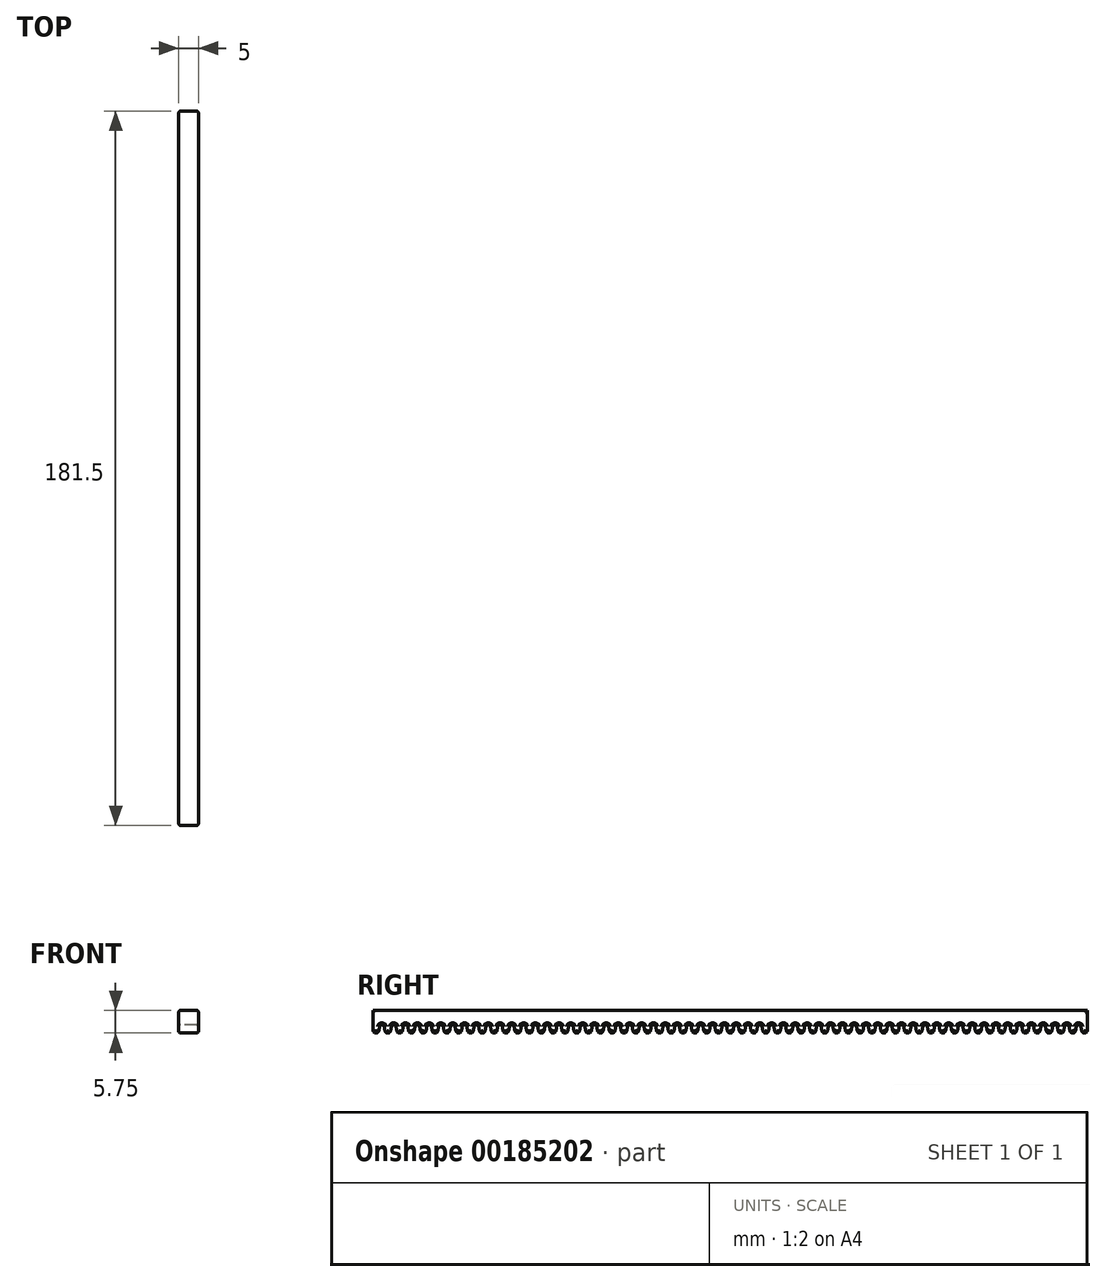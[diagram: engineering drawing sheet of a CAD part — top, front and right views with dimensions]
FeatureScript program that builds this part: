
annotation { "Feature Type Name" : "Feature", "Feature Type Description" : "" }
export const myFeature = defineFeature(function(context is Context, id is Id, definition is map)
    precondition{}
    {
        {
            var Q0;
            Q0=qCreatedBy(makeId("Right.planeOp"),FACE);
            var sketch = newSketch(context, id + "F0", { "sketchPlane" : qUnion([Q0])});
            skArc(sketch, "E0", {"start": v(-0.75, 0) * mm, "mid": v(-0.06, -0.75) * mm, "end": v(0.74, -0.13) * mm});
            skArc(sketch, "E1", {"start": v(2.1, 0.85) * mm, "mid": v(1.5, 1.35) * mm, "end": v(0.9, 0.85) * mm});
            skLineSegment(sketch, "E2", {"start": v(0.9, 0.85) * mm, "end": v(0.74, -0.13) * mm});
            skArc(sketch, "E3", {"start": v(2.26, -0.13) * mm, "mid": v(3, -0.75) * mm, "end": v(3.74, -0.13) * mm});
            skArc(sketch, "E4", {"start": v(5.1, 0.85) * mm, "mid": v(4.5, 1.35) * mm, "end": v(3.9, 0.85) * mm});
            skArc(sketch, "E5", {"start": v(5.26, -0.13) * mm, "mid": v(6.06, -0.75) * mm, "end": v(6.75, 0) * mm});
            skLineSegment(sketch, "E6", {"start": v(2.1, 0.85) * mm, "end": v(2.26, -0.13) * mm});
            skLineSegment(sketch, "E7", {"start": v(3.9, 0.85) * mm, "end": v(3.74, -0.13) * mm});
            skLineSegment(sketch, "E8", {"start": v(5.1, 0.85) * mm, "end": v(5.26, -0.13) * mm});
            skLineSegment(sketch, "E9", {"start": v(-0.75, 0) * mm, "end": v(-0.75, 5) * mm});
            skLineSegment(sketch, "E10", {"start": v(-0.75, 5) * mm, "end": v(180.75, 5) * mm});
            skArc(sketch, "E11.1.0.0", {"start": v(11.1, 0.85) * mm, "mid": v(10.5, 1.35) * mm, "end": v(9.9, 0.85) * mm});
            skLineSegment(sketch, "E11.1.0.1", {"start": v(11.1, 0.85) * mm, "end": v(11.26, -0.13) * mm});
            skArc(sketch, "E11.1.0.2", {"start": v(5.25, 0) * mm, "mid": v(5.94, -0.75) * mm, "end": v(6.74, -0.13) * mm});
            skArc(sketch, "E11.1.0.3", {"start": v(8.26, -0.13) * mm, "mid": v(9, -0.75) * mm, "end": v(9.74, -0.13) * mm});
            skLineSegment(sketch, "E11.1.0.4", {"start": v(8.1, 0.85) * mm, "end": v(8.26, -0.13) * mm});
            skArc(sketch, "E11.1.0.5", {"start": v(8.1, 0.85) * mm, "mid": v(7.5, 1.35) * mm, "end": v(6.9, 0.85) * mm});
            skLineSegment(sketch, "E11.1.0.6", {"start": v(9.9, 0.85) * mm, "end": v(9.74, -0.13) * mm});
            skArc(sketch, "E11.1.0.7", {"start": v(11.26, -0.13) * mm, "mid": v(12.06, -0.75) * mm, "end": v(12.75, 0) * mm});
            skLineSegment(sketch, "E11.1.0.8", {"start": v(6.9, 0.85) * mm, "end": v(6.74, -0.13) * mm});
            skArc(sketch, "E11.2.0.0", {"start": v(17.1, 0.85) * mm, "mid": v(16.5, 1.35) * mm, "end": v(15.9, 0.85) * mm});
            skLineSegment(sketch, "E11.2.0.1", {"start": v(17.1, 0.85) * mm, "end": v(17.26, -0.13) * mm});
            skArc(sketch, "E11.2.0.2", {"start": v(11.25, 0) * mm, "mid": v(11.94, -0.75) * mm, "end": v(12.74, -0.13) * mm});
            skArc(sketch, "E11.2.0.3", {"start": v(14.26, -0.13) * mm, "mid": v(15, -0.75) * mm, "end": v(15.74, -0.13) * mm});
            skLineSegment(sketch, "E11.2.0.4", {"start": v(14.1, 0.85) * mm, "end": v(14.26, -0.13) * mm});
            skArc(sketch, "E11.2.0.5", {"start": v(14.1, 0.85) * mm, "mid": v(13.5, 1.35) * mm, "end": v(12.9, 0.85) * mm});
            skLineSegment(sketch, "E11.2.0.6", {"start": v(15.9, 0.85) * mm, "end": v(15.74, -0.13) * mm});
            skArc(sketch, "E11.2.0.7", {"start": v(17.26, -0.13) * mm, "mid": v(18.06, -0.75) * mm, "end": v(18.75, 0) * mm});
            skLineSegment(sketch, "E11.2.0.8", {"start": v(12.9, 0.85) * mm, "end": v(12.74, -0.13) * mm});
            skArc(sketch, "E11.3.0.0", {"start": v(23.1, 0.85) * mm, "mid": v(22.5, 1.35) * mm, "end": v(21.9, 0.85) * mm});
            skLineSegment(sketch, "E11.3.0.1", {"start": v(23.1, 0.85) * mm, "end": v(23.26, -0.13) * mm});
            skArc(sketch, "E11.3.0.2", {"start": v(17.25, 0) * mm, "mid": v(17.94, -0.75) * mm, "end": v(18.74, -0.13) * mm});
            skArc(sketch, "E11.3.0.3", {"start": v(20.26, -0.13) * mm, "mid": v(21, -0.75) * mm, "end": v(21.74, -0.13) * mm});
            skLineSegment(sketch, "E11.3.0.4", {"start": v(20.1, 0.85) * mm, "end": v(20.26, -0.13) * mm});
            skArc(sketch, "E11.3.0.5", {"start": v(20.1, 0.85) * mm, "mid": v(19.5, 1.35) * mm, "end": v(18.9, 0.85) * mm});
            skLineSegment(sketch, "E11.3.0.6", {"start": v(21.9, 0.85) * mm, "end": v(21.74, -0.13) * mm});
            skArc(sketch, "E11.3.0.7", {"start": v(23.26, -0.13) * mm, "mid": v(24.06, -0.75) * mm, "end": v(24.75, 0) * mm});
            skLineSegment(sketch, "E11.3.0.8", {"start": v(18.9, 0.85) * mm, "end": v(18.74, -0.13) * mm});
            skArc(sketch, "E11.4.0.0", {"start": v(29.1, 0.85) * mm, "mid": v(28.5, 1.35) * mm, "end": v(27.9, 0.85) * mm});
            skLineSegment(sketch, "E11.4.0.1", {"start": v(29.1, 0.85) * mm, "end": v(29.26, -0.13) * mm});
            skArc(sketch, "E11.4.0.2", {"start": v(23.25, 0) * mm, "mid": v(23.94, -0.75) * mm, "end": v(24.74, -0.13) * mm});
            skArc(sketch, "E11.4.0.3", {"start": v(26.26, -0.13) * mm, "mid": v(27, -0.75) * mm, "end": v(27.74, -0.13) * mm});
            skLineSegment(sketch, "E11.4.0.4", {"start": v(26.1, 0.85) * mm, "end": v(26.26, -0.13) * mm});
            skArc(sketch, "E11.4.0.5", {"start": v(26.1, 0.85) * mm, "mid": v(25.5, 1.35) * mm, "end": v(24.9, 0.85) * mm});
            skLineSegment(sketch, "E11.4.0.6", {"start": v(27.9, 0.85) * mm, "end": v(27.74, -0.13) * mm});
            skArc(sketch, "E11.4.0.7", {"start": v(29.26, -0.13) * mm, "mid": v(30.06, -0.75) * mm, "end": v(30.75, 0) * mm});
            skLineSegment(sketch, "E11.4.0.8", {"start": v(24.9, 0.85) * mm, "end": v(24.74, -0.13) * mm});
            skArc(sketch, "E11.5.0.0", {"start": v(35.1, 0.85) * mm, "mid": v(34.5, 1.35) * mm, "end": v(33.9, 0.85) * mm});
            skLineSegment(sketch, "E11.5.0.1", {"start": v(35.1, 0.85) * mm, "end": v(35.26, -0.13) * mm});
            skArc(sketch, "E11.5.0.2", {"start": v(29.25, 0) * mm, "mid": v(29.94, -0.75) * mm, "end": v(30.74, -0.13) * mm});
            skArc(sketch, "E11.5.0.3", {"start": v(32.26, -0.13) * mm, "mid": v(33, -0.75) * mm, "end": v(33.74, -0.13) * mm});
            skLineSegment(sketch, "E11.5.0.4", {"start": v(32.1, 0.85) * mm, "end": v(32.26, -0.13) * mm});
            skArc(sketch, "E11.5.0.5", {"start": v(32.1, 0.85) * mm, "mid": v(31.5, 1.35) * mm, "end": v(30.9, 0.85) * mm});
            skLineSegment(sketch, "E11.5.0.6", {"start": v(33.9, 0.85) * mm, "end": v(33.74, -0.13) * mm});
            skArc(sketch, "E11.5.0.7", {"start": v(35.26, -0.13) * mm, "mid": v(36.06, -0.75) * mm, "end": v(36.75, 0) * mm});
            skLineSegment(sketch, "E11.5.0.8", {"start": v(30.9, 0.85) * mm, "end": v(30.74, -0.13) * mm});
            skArc(sketch, "E11.6.0.0", {"start": v(41.1, 0.85) * mm, "mid": v(40.5, 1.35) * mm, "end": v(39.9, 0.85) * mm});
            skLineSegment(sketch, "E11.6.0.1", {"start": v(41.1, 0.85) * mm, "end": v(41.26, -0.13) * mm});
            skArc(sketch, "E11.6.0.2", {"start": v(35.25, 0) * mm, "mid": v(35.94, -0.75) * mm, "end": v(36.74, -0.13) * mm});
            skArc(sketch, "E11.6.0.3", {"start": v(38.26, -0.13) * mm, "mid": v(39, -0.75) * mm, "end": v(39.74, -0.13) * mm});
            skLineSegment(sketch, "E11.6.0.4", {"start": v(38.1, 0.85) * mm, "end": v(38.26, -0.13) * mm});
            skArc(sketch, "E11.6.0.5", {"start": v(38.1, 0.85) * mm, "mid": v(37.5, 1.35) * mm, "end": v(36.9, 0.85) * mm});
            skLineSegment(sketch, "E11.6.0.6", {"start": v(39.9, 0.85) * mm, "end": v(39.74, -0.13) * mm});
            skArc(sketch, "E11.6.0.7", {"start": v(41.26, -0.13) * mm, "mid": v(42.06, -0.75) * mm, "end": v(42.75, 0) * mm});
            skLineSegment(sketch, "E11.6.0.8", {"start": v(36.9, 0.85) * mm, "end": v(36.74, -0.13) * mm});
            skArc(sketch, "E11.7.0.0", {"start": v(47.1, 0.85) * mm, "mid": v(46.5, 1.35) * mm, "end": v(45.9, 0.85) * mm});
            skLineSegment(sketch, "E11.7.0.1", {"start": v(47.1, 0.85) * mm, "end": v(47.26, -0.13) * mm});
            skArc(sketch, "E11.7.0.2", {"start": v(41.25, 0) * mm, "mid": v(41.94, -0.75) * mm, "end": v(42.74, -0.13) * mm});
            skArc(sketch, "E11.7.0.3", {"start": v(44.26, -0.13) * mm, "mid": v(45, -0.75) * mm, "end": v(45.74, -0.13) * mm});
            skLineSegment(sketch, "E11.7.0.4", {"start": v(44.1, 0.85) * mm, "end": v(44.26, -0.13) * mm});
            skArc(sketch, "E11.7.0.5", {"start": v(44.1, 0.85) * mm, "mid": v(43.5, 1.35) * mm, "end": v(42.9, 0.85) * mm});
            skLineSegment(sketch, "E11.7.0.6", {"start": v(45.9, 0.85) * mm, "end": v(45.74, -0.13) * mm});
            skArc(sketch, "E11.7.0.7", {"start": v(47.26, -0.13) * mm, "mid": v(48.06, -0.75) * mm, "end": v(48.75, 0) * mm});
            skLineSegment(sketch, "E11.7.0.8", {"start": v(42.9, 0.85) * mm, "end": v(42.74, -0.13) * mm});
            skArc(sketch, "E11.8.0.0", {"start": v(53.1, 0.85) * mm, "mid": v(52.5, 1.35) * mm, "end": v(51.9, 0.85) * mm});
            skLineSegment(sketch, "E11.8.0.1", {"start": v(53.1, 0.85) * mm, "end": v(53.26, -0.13) * mm});
            skArc(sketch, "E11.8.0.2", {"start": v(47.25, 0) * mm, "mid": v(47.94, -0.75) * mm, "end": v(48.74, -0.13) * mm});
            skArc(sketch, "E11.8.0.3", {"start": v(50.26, -0.13) * mm, "mid": v(51, -0.75) * mm, "end": v(51.74, -0.13) * mm});
            skLineSegment(sketch, "E11.8.0.4", {"start": v(50.1, 0.85) * mm, "end": v(50.26, -0.13) * mm});
            skArc(sketch, "E11.8.0.5", {"start": v(50.1, 0.85) * mm, "mid": v(49.5, 1.35) * mm, "end": v(48.9, 0.85) * mm});
            skLineSegment(sketch, "E11.8.0.6", {"start": v(51.9, 0.85) * mm, "end": v(51.74, -0.13) * mm});
            skArc(sketch, "E11.8.0.7", {"start": v(53.26, -0.13) * mm, "mid": v(54.06, -0.75) * mm, "end": v(54.75, 0) * mm});
            skLineSegment(sketch, "E11.8.0.8", {"start": v(48.9, 0.85) * mm, "end": v(48.74, -0.13) * mm});
            skArc(sketch, "E11.9.0.0", {"start": v(59.1, 0.85) * mm, "mid": v(58.5, 1.35) * mm, "end": v(57.9, 0.85) * mm});
            skLineSegment(sketch, "E11.9.0.1", {"start": v(59.1, 0.85) * mm, "end": v(59.26, -0.13) * mm});
            skArc(sketch, "E11.9.0.2", {"start": v(53.25, 0) * mm, "mid": v(53.94, -0.75) * mm, "end": v(54.74, -0.13) * mm});
            skArc(sketch, "E11.9.0.3", {"start": v(56.26, -0.13) * mm, "mid": v(57, -0.75) * mm, "end": v(57.74, -0.13) * mm});
            skLineSegment(sketch, "E11.9.0.4", {"start": v(56.1, 0.85) * mm, "end": v(56.26, -0.13) * mm});
            skArc(sketch, "E11.9.0.5", {"start": v(56.1, 0.85) * mm, "mid": v(55.5, 1.35) * mm, "end": v(54.9, 0.85) * mm});
            skLineSegment(sketch, "E11.9.0.6", {"start": v(57.9, 0.85) * mm, "end": v(57.74, -0.13) * mm});
            skArc(sketch, "E11.9.0.7", {"start": v(59.26, -0.13) * mm, "mid": v(60.06, -0.75) * mm, "end": v(60.75, 0) * mm});
            skLineSegment(sketch, "E11.9.0.8", {"start": v(54.9, 0.85) * mm, "end": v(54.74, -0.13) * mm});
            skArc(sketch, "E11.10.0.0", {"start": v(65.1, 0.85) * mm, "mid": v(64.5, 1.35) * mm, "end": v(63.9, 0.85) * mm});
            skLineSegment(sketch, "E11.10.0.1", {"start": v(65.1, 0.85) * mm, "end": v(65.26, -0.13) * mm});
            skArc(sketch, "E11.10.0.2", {"start": v(59.25, 0) * mm, "mid": v(59.94, -0.75) * mm, "end": v(60.74, -0.13) * mm});
            skArc(sketch, "E11.10.0.3", {"start": v(62.26, -0.13) * mm, "mid": v(63, -0.75) * mm, "end": v(63.74, -0.13) * mm});
            skLineSegment(sketch, "E11.10.0.4", {"start": v(62.1, 0.85) * mm, "end": v(62.26, -0.13) * mm});
            skArc(sketch, "E11.10.0.5", {"start": v(62.1, 0.85) * mm, "mid": v(61.5, 1.35) * mm, "end": v(60.9, 0.85) * mm});
            skLineSegment(sketch, "E11.10.0.6", {"start": v(63.9, 0.85) * mm, "end": v(63.74, -0.13) * mm});
            skArc(sketch, "E11.10.0.7", {"start": v(65.26, -0.13) * mm, "mid": v(66.06, -0.75) * mm, "end": v(66.75, 0) * mm});
            skLineSegment(sketch, "E11.10.0.8", {"start": v(60.9, 0.85) * mm, "end": v(60.74, -0.13) * mm});
            skArc(sketch, "E11.11.0.0", {"start": v(71.1, 0.85) * mm, "mid": v(70.5, 1.35) * mm, "end": v(69.9, 0.85) * mm});
            skLineSegment(sketch, "E11.11.0.1", {"start": v(71.1, 0.85) * mm, "end": v(71.26, -0.13) * mm});
            skArc(sketch, "E11.11.0.2", {"start": v(65.25, 0) * mm, "mid": v(65.94, -0.75) * mm, "end": v(66.74, -0.13) * mm});
            skArc(sketch, "E11.11.0.3", {"start": v(68.26, -0.13) * mm, "mid": v(69, -0.75) * mm, "end": v(69.74, -0.13) * mm});
            skLineSegment(sketch, "E11.11.0.4", {"start": v(68.1, 0.85) * mm, "end": v(68.26, -0.13) * mm});
            skArc(sketch, "E11.11.0.5", {"start": v(68.1, 0.85) * mm, "mid": v(67.5, 1.35) * mm, "end": v(66.9, 0.85) * mm});
            skLineSegment(sketch, "E11.11.0.6", {"start": v(69.9, 0.85) * mm, "end": v(69.74, -0.13) * mm});
            skArc(sketch, "E11.11.0.7", {"start": v(71.26, -0.13) * mm, "mid": v(72.06, -0.75) * mm, "end": v(72.75, 0) * mm});
            skLineSegment(sketch, "E11.11.0.8", {"start": v(66.9, 0.85) * mm, "end": v(66.74, -0.13) * mm});
            skArc(sketch, "E11.12.0.0", {"start": v(77.1, 0.85) * mm, "mid": v(76.5, 1.35) * mm, "end": v(75.9, 0.85) * mm});
            skLineSegment(sketch, "E11.12.0.1", {"start": v(77.1, 0.85) * mm, "end": v(77.26, -0.13) * mm});
            skArc(sketch, "E11.12.0.2", {"start": v(71.25, 0) * mm, "mid": v(71.94, -0.75) * mm, "end": v(72.74, -0.13) * mm});
            skArc(sketch, "E11.12.0.3", {"start": v(74.26, -0.13) * mm, "mid": v(75, -0.75) * mm, "end": v(75.74, -0.13) * mm});
            skLineSegment(sketch, "E11.12.0.4", {"start": v(74.1, 0.85) * mm, "end": v(74.26, -0.13) * mm});
            skArc(sketch, "E11.12.0.5", {"start": v(74.1, 0.85) * mm, "mid": v(73.5, 1.35) * mm, "end": v(72.9, 0.85) * mm});
            skLineSegment(sketch, "E11.12.0.6", {"start": v(75.9, 0.85) * mm, "end": v(75.74, -0.13) * mm});
            skArc(sketch, "E11.12.0.7", {"start": v(77.26, -0.13) * mm, "mid": v(78.06, -0.75) * mm, "end": v(78.75, 0) * mm});
            skLineSegment(sketch, "E11.12.0.8", {"start": v(72.9, 0.85) * mm, "end": v(72.74, -0.13) * mm});
            skArc(sketch, "E11.13.0.0", {"start": v(83.1, 0.85) * mm, "mid": v(82.5, 1.35) * mm, "end": v(81.9, 0.85) * mm});
            skLineSegment(sketch, "E11.13.0.1", {"start": v(83.1, 0.85) * mm, "end": v(83.26, -0.13) * mm});
            skArc(sketch, "E11.13.0.2", {"start": v(77.25, 0) * mm, "mid": v(77.94, -0.75) * mm, "end": v(78.74, -0.13) * mm});
            skArc(sketch, "E11.13.0.3", {"start": v(80.26, -0.13) * mm, "mid": v(81, -0.75) * mm, "end": v(81.74, -0.13) * mm});
            skLineSegment(sketch, "E11.13.0.4", {"start": v(80.1, 0.85) * mm, "end": v(80.26, -0.13) * mm});
            skArc(sketch, "E11.13.0.5", {"start": v(80.1, 0.85) * mm, "mid": v(79.5, 1.35) * mm, "end": v(78.9, 0.85) * mm});
            skLineSegment(sketch, "E11.13.0.6", {"start": v(81.9, 0.85) * mm, "end": v(81.74, -0.13) * mm});
            skArc(sketch, "E11.13.0.7", {"start": v(83.26, -0.13) * mm, "mid": v(84.06, -0.75) * mm, "end": v(84.75, 0) * mm});
            skLineSegment(sketch, "E11.13.0.8", {"start": v(78.9, 0.85) * mm, "end": v(78.74, -0.13) * mm});
            skArc(sketch, "E11.14.0.0", {"start": v(89.1, 0.85) * mm, "mid": v(88.5, 1.35) * mm, "end": v(87.9, 0.85) * mm});
            skLineSegment(sketch, "E11.14.0.1", {"start": v(89.1, 0.85) * mm, "end": v(89.26, -0.13) * mm});
            skArc(sketch, "E11.14.0.2", {"start": v(83.25, 0) * mm, "mid": v(83.94, -0.75) * mm, "end": v(84.74, -0.13) * mm});
            skArc(sketch, "E11.14.0.3", {"start": v(86.26, -0.13) * mm, "mid": v(87, -0.75) * mm, "end": v(87.74, -0.13) * mm});
            skLineSegment(sketch, "E11.14.0.4", {"start": v(86.1, 0.85) * mm, "end": v(86.26, -0.13) * mm});
            skArc(sketch, "E11.14.0.5", {"start": v(86.1, 0.85) * mm, "mid": v(85.5, 1.35) * mm, "end": v(84.9, 0.85) * mm});
            skLineSegment(sketch, "E11.14.0.6", {"start": v(87.9, 0.85) * mm, "end": v(87.74, -0.13) * mm});
            skArc(sketch, "E11.14.0.7", {"start": v(89.26, -0.13) * mm, "mid": v(90.06, -0.75) * mm, "end": v(90.75, 0) * mm});
            skLineSegment(sketch, "E11.14.0.8", {"start": v(84.9, 0.85) * mm, "end": v(84.74, -0.13) * mm});
            skArc(sketch, "E11.15.0.0", {"start": v(95.1, 0.85) * mm, "mid": v(94.5, 1.35) * mm, "end": v(93.9, 0.85) * mm});
            skLineSegment(sketch, "E11.15.0.1", {"start": v(95.1, 0.85) * mm, "end": v(95.26, -0.13) * mm});
            skArc(sketch, "E11.15.0.2", {"start": v(89.25, 0) * mm, "mid": v(89.94, -0.75) * mm, "end": v(90.74, -0.13) * mm});
            skArc(sketch, "E11.15.0.3", {"start": v(92.26, -0.13) * mm, "mid": v(93, -0.75) * mm, "end": v(93.74, -0.13) * mm});
            skLineSegment(sketch, "E11.15.0.4", {"start": v(92.1, 0.85) * mm, "end": v(92.26, -0.13) * mm});
            skArc(sketch, "E11.15.0.5", {"start": v(92.1, 0.85) * mm, "mid": v(91.5, 1.35) * mm, "end": v(90.9, 0.85) * mm});
            skLineSegment(sketch, "E11.15.0.6", {"start": v(93.9, 0.85) * mm, "end": v(93.74, -0.13) * mm});
            skArc(sketch, "E11.15.0.7", {"start": v(95.26, -0.13) * mm, "mid": v(96.06, -0.75) * mm, "end": v(96.75, 0) * mm});
            skLineSegment(sketch, "E11.15.0.8", {"start": v(90.9, 0.85) * mm, "end": v(90.74, -0.13) * mm});
            skArc(sketch, "E11.16.0.0", {"start": v(101.1, 0.85) * mm, "mid": v(100.5, 1.35) * mm, "end": v(99.9, 0.85) * mm});
            skLineSegment(sketch, "E11.16.0.1", {"start": v(101.1, 0.85) * mm, "end": v(101.26, -0.13) * mm});
            skArc(sketch, "E11.16.0.2", {"start": v(95.25, 0) * mm, "mid": v(95.94, -0.75) * mm, "end": v(96.74, -0.13) * mm});
            skArc(sketch, "E11.16.0.3", {"start": v(98.26, -0.13) * mm, "mid": v(99, -0.75) * mm, "end": v(99.74, -0.13) * mm});
            skLineSegment(sketch, "E11.16.0.4", {"start": v(98.1, 0.85) * mm, "end": v(98.26, -0.13) * mm});
            skArc(sketch, "E11.16.0.5", {"start": v(98.1, 0.85) * mm, "mid": v(97.5, 1.35) * mm, "end": v(96.9, 0.85) * mm});
            skLineSegment(sketch, "E11.16.0.6", {"start": v(99.9, 0.85) * mm, "end": v(99.74, -0.13) * mm});
            skArc(sketch, "E11.16.0.7", {"start": v(101.26, -0.13) * mm, "mid": v(102.06, -0.75) * mm, "end": v(102.75, 0) * mm});
            skLineSegment(sketch, "E11.16.0.8", {"start": v(96.9, 0.85) * mm, "end": v(96.74, -0.13) * mm});
            skArc(sketch, "E11.17.0.0", {"start": v(107.1, 0.85) * mm, "mid": v(106.5, 1.35) * mm, "end": v(105.9, 0.85) * mm});
            skLineSegment(sketch, "E11.17.0.1", {"start": v(107.1, 0.85) * mm, "end": v(107.26, -0.13) * mm});
            skArc(sketch, "E11.17.0.2", {"start": v(101.25, 0) * mm, "mid": v(101.94, -0.75) * mm, "end": v(102.74, -0.13) * mm});
            skArc(sketch, "E11.17.0.3", {"start": v(104.26, -0.13) * mm, "mid": v(105, -0.75) * mm, "end": v(105.74, -0.13) * mm});
            skLineSegment(sketch, "E11.17.0.4", {"start": v(104.1, 0.85) * mm, "end": v(104.26, -0.13) * mm});
            skArc(sketch, "E11.17.0.5", {"start": v(104.1, 0.85) * mm, "mid": v(103.5, 1.35) * mm, "end": v(102.9, 0.85) * mm});
            skLineSegment(sketch, "E11.17.0.6", {"start": v(105.9, 0.85) * mm, "end": v(105.74, -0.13) * mm});
            skArc(sketch, "E11.17.0.7", {"start": v(107.26, -0.13) * mm, "mid": v(108.06, -0.75) * mm, "end": v(108.75, 0) * mm});
            skLineSegment(sketch, "E11.17.0.8", {"start": v(102.9, 0.85) * mm, "end": v(102.74, -0.13) * mm});
            skArc(sketch, "E11.18.0.0", {"start": v(113.1, 0.85) * mm, "mid": v(112.5, 1.35) * mm, "end": v(111.9, 0.85) * mm});
            skLineSegment(sketch, "E11.18.0.1", {"start": v(113.1, 0.85) * mm, "end": v(113.26, -0.13) * mm});
            skArc(sketch, "E11.18.0.2", {"start": v(107.25, 0) * mm, "mid": v(107.94, -0.75) * mm, "end": v(108.74, -0.13) * mm});
            skArc(sketch, "E11.18.0.3", {"start": v(110.26, -0.13) * mm, "mid": v(111, -0.75) * mm, "end": v(111.74, -0.13) * mm});
            skLineSegment(sketch, "E11.18.0.4", {"start": v(110.1, 0.85) * mm, "end": v(110.26, -0.13) * mm});
            skArc(sketch, "E11.18.0.5", {"start": v(110.1, 0.85) * mm, "mid": v(109.5, 1.35) * mm, "end": v(108.9, 0.85) * mm});
            skLineSegment(sketch, "E11.18.0.6", {"start": v(111.9, 0.85) * mm, "end": v(111.74, -0.13) * mm});
            skArc(sketch, "E11.18.0.7", {"start": v(113.26, -0.13) * mm, "mid": v(114.06, -0.75) * mm, "end": v(114.75, 0) * mm});
            skLineSegment(sketch, "E11.18.0.8", {"start": v(108.9, 0.85) * mm, "end": v(108.74, -0.13) * mm});
            skArc(sketch, "E11.19.0.0", {"start": v(119.1, 0.85) * mm, "mid": v(118.5, 1.35) * mm, "end": v(117.9, 0.85) * mm});
            skLineSegment(sketch, "E11.19.0.1", {"start": v(119.1, 0.85) * mm, "end": v(119.26, -0.13) * mm});
            skArc(sketch, "E11.19.0.2", {"start": v(113.25, 0) * mm, "mid": v(113.94, -0.75) * mm, "end": v(114.74, -0.13) * mm});
            skArc(sketch, "E11.19.0.3", {"start": v(116.26, -0.13) * mm, "mid": v(117, -0.75) * mm, "end": v(117.74, -0.13) * mm});
            skLineSegment(sketch, "E11.19.0.4", {"start": v(116.1, 0.85) * mm, "end": v(116.26, -0.13) * mm});
            skArc(sketch, "E11.19.0.5", {"start": v(116.1, 0.85) * mm, "mid": v(115.5, 1.35) * mm, "end": v(114.9, 0.85) * mm});
            skLineSegment(sketch, "E11.19.0.6", {"start": v(117.9, 0.85) * mm, "end": v(117.74, -0.13) * mm});
            skArc(sketch, "E11.19.0.7", {"start": v(119.26, -0.13) * mm, "mid": v(120.06, -0.75) * mm, "end": v(120.75, 0) * mm});
            skLineSegment(sketch, "E11.19.0.8", {"start": v(114.9, 0.85) * mm, "end": v(114.74, -0.13) * mm});
            skArc(sketch, "E11.20.0.0", {"start": v(125.1, 0.85) * mm, "mid": v(124.5, 1.35) * mm, "end": v(123.9, 0.85) * mm});
            skLineSegment(sketch, "E11.20.0.1", {"start": v(125.1, 0.85) * mm, "end": v(125.26, -0.13) * mm});
            skArc(sketch, "E11.20.0.2", {"start": v(119.25, 0) * mm, "mid": v(119.94, -0.75) * mm, "end": v(120.74, -0.13) * mm});
            skArc(sketch, "E11.20.0.3", {"start": v(122.26, -0.13) * mm, "mid": v(123, -0.75) * mm, "end": v(123.74, -0.13) * mm});
            skLineSegment(sketch, "E11.20.0.4", {"start": v(122.1, 0.85) * mm, "end": v(122.26, -0.13) * mm});
            skArc(sketch, "E11.20.0.5", {"start": v(122.1, 0.85) * mm, "mid": v(121.5, 1.35) * mm, "end": v(120.9, 0.85) * mm});
            skLineSegment(sketch, "E11.20.0.6", {"start": v(123.9, 0.85) * mm, "end": v(123.74, -0.13) * mm});
            skArc(sketch, "E11.20.0.7", {"start": v(125.26, -0.13) * mm, "mid": v(126.06, -0.75) * mm, "end": v(126.75, 0) * mm});
            skLineSegment(sketch, "E11.20.0.8", {"start": v(120.9, 0.85) * mm, "end": v(120.74, -0.13) * mm});
            skArc(sketch, "E11.21.0.0", {"start": v(131.1, 0.85) * mm, "mid": v(130.5, 1.35) * mm, "end": v(129.9, 0.85) * mm});
            skLineSegment(sketch, "E11.21.0.1", {"start": v(131.1, 0.85) * mm, "end": v(131.26, -0.13) * mm});
            skArc(sketch, "E11.21.0.2", {"start": v(125.25, 0) * mm, "mid": v(125.94, -0.75) * mm, "end": v(126.74, -0.13) * mm});
            skArc(sketch, "E11.21.0.3", {"start": v(128.26, -0.13) * mm, "mid": v(129, -0.75) * mm, "end": v(129.74, -0.13) * mm});
            skLineSegment(sketch, "E11.21.0.4", {"start": v(128.1, 0.85) * mm, "end": v(128.26, -0.13) * mm});
            skArc(sketch, "E11.21.0.5", {"start": v(128.1, 0.85) * mm, "mid": v(127.5, 1.35) * mm, "end": v(126.9, 0.85) * mm});
            skLineSegment(sketch, "E11.21.0.6", {"start": v(129.9, 0.85) * mm, "end": v(129.74, -0.13) * mm});
            skArc(sketch, "E11.21.0.7", {"start": v(131.26, -0.13) * mm, "mid": v(132.06, -0.75) * mm, "end": v(132.75, 0) * mm});
            skLineSegment(sketch, "E11.21.0.8", {"start": v(126.9, 0.85) * mm, "end": v(126.74, -0.13) * mm});
            skArc(sketch, "E11.22.0.0", {"start": v(137.1, 0.85) * mm, "mid": v(136.5, 1.35) * mm, "end": v(135.9, 0.85) * mm});
            skLineSegment(sketch, "E11.22.0.1", {"start": v(137.1, 0.85) * mm, "end": v(137.26, -0.13) * mm});
            skArc(sketch, "E11.22.0.2", {"start": v(131.25, 0) * mm, "mid": v(131.94, -0.75) * mm, "end": v(132.74, -0.13) * mm});
            skArc(sketch, "E11.22.0.3", {"start": v(134.26, -0.13) * mm, "mid": v(135, -0.75) * mm, "end": v(135.74, -0.13) * mm});
            skLineSegment(sketch, "E11.22.0.4", {"start": v(134.1, 0.85) * mm, "end": v(134.26, -0.13) * mm});
            skArc(sketch, "E11.22.0.5", {"start": v(134.1, 0.85) * mm, "mid": v(133.5, 1.35) * mm, "end": v(132.9, 0.85) * mm});
            skLineSegment(sketch, "E11.22.0.6", {"start": v(135.9, 0.85) * mm, "end": v(135.74, -0.13) * mm});
            skArc(sketch, "E11.22.0.7", {"start": v(137.26, -0.13) * mm, "mid": v(138.06, -0.75) * mm, "end": v(138.75, 0) * mm});
            skLineSegment(sketch, "E11.22.0.8", {"start": v(132.9, 0.85) * mm, "end": v(132.74, -0.13) * mm});
            skArc(sketch, "E11.23.0.0", {"start": v(143.1, 0.85) * mm, "mid": v(142.5, 1.35) * mm, "end": v(141.9, 0.85) * mm});
            skLineSegment(sketch, "E11.23.0.1", {"start": v(143.1, 0.85) * mm, "end": v(143.26, -0.13) * mm});
            skArc(sketch, "E11.23.0.2", {"start": v(137.25, 0) * mm, "mid": v(137.94, -0.75) * mm, "end": v(138.74, -0.13) * mm});
            skArc(sketch, "E11.23.0.3", {"start": v(140.26, -0.13) * mm, "mid": v(141, -0.75) * mm, "end": v(141.74, -0.13) * mm});
            skLineSegment(sketch, "E11.23.0.4", {"start": v(140.1, 0.85) * mm, "end": v(140.26, -0.13) * mm});
            skArc(sketch, "E11.23.0.5", {"start": v(140.1, 0.85) * mm, "mid": v(139.5, 1.35) * mm, "end": v(138.9, 0.85) * mm});
            skLineSegment(sketch, "E11.23.0.6", {"start": v(141.9, 0.85) * mm, "end": v(141.74, -0.13) * mm});
            skArc(sketch, "E11.23.0.7", {"start": v(143.26, -0.13) * mm, "mid": v(144.06, -0.75) * mm, "end": v(144.75, 0) * mm});
            skLineSegment(sketch, "E11.23.0.8", {"start": v(138.9, 0.85) * mm, "end": v(138.74, -0.13) * mm});
            skArc(sketch, "E11.24.0.0", {"start": v(149.1, 0.85) * mm, "mid": v(148.5, 1.35) * mm, "end": v(147.9, 0.85) * mm});
            skLineSegment(sketch, "E11.24.0.1", {"start": v(149.1, 0.85) * mm, "end": v(149.26, -0.13) * mm});
            skArc(sketch, "E11.24.0.2", {"start": v(143.25, 0) * mm, "mid": v(143.94, -0.75) * mm, "end": v(144.74, -0.13) * mm});
            skArc(sketch, "E11.24.0.3", {"start": v(146.26, -0.13) * mm, "mid": v(147, -0.75) * mm, "end": v(147.74, -0.13) * mm});
            skLineSegment(sketch, "E11.24.0.4", {"start": v(146.1, 0.85) * mm, "end": v(146.26, -0.13) * mm});
            skArc(sketch, "E11.24.0.5", {"start": v(146.1, 0.85) * mm, "mid": v(145.5, 1.35) * mm, "end": v(144.9, 0.85) * mm});
            skLineSegment(sketch, "E11.24.0.6", {"start": v(147.9, 0.85) * mm, "end": v(147.74, -0.13) * mm});
            skArc(sketch, "E11.24.0.7", {"start": v(149.26, -0.13) * mm, "mid": v(150.06, -0.75) * mm, "end": v(150.75, 0) * mm});
            skLineSegment(sketch, "E11.24.0.8", {"start": v(144.9, 0.85) * mm, "end": v(144.74, -0.13) * mm});
            skArc(sketch, "E11.25.0.0", {"start": v(155.1, 0.85) * mm, "mid": v(154.5, 1.35) * mm, "end": v(153.9, 0.85) * mm});
            skLineSegment(sketch, "E11.25.0.1", {"start": v(155.1, 0.85) * mm, "end": v(155.26, -0.13) * mm});
            skArc(sketch, "E11.25.0.2", {"start": v(149.25, 0) * mm, "mid": v(149.94, -0.75) * mm, "end": v(150.74, -0.13) * mm});
            skArc(sketch, "E11.25.0.3", {"start": v(152.26, -0.13) * mm, "mid": v(153, -0.75) * mm, "end": v(153.74, -0.13) * mm});
            skLineSegment(sketch, "E11.25.0.4", {"start": v(152.1, 0.85) * mm, "end": v(152.26, -0.13) * mm});
            skArc(sketch, "E11.25.0.5", {"start": v(152.1, 0.85) * mm, "mid": v(151.5, 1.35) * mm, "end": v(150.9, 0.85) * mm});
            skLineSegment(sketch, "E11.25.0.6", {"start": v(153.9, 0.85) * mm, "end": v(153.74, -0.13) * mm});
            skArc(sketch, "E11.25.0.7", {"start": v(155.26, -0.13) * mm, "mid": v(156.06, -0.75) * mm, "end": v(156.75, 0) * mm});
            skLineSegment(sketch, "E11.25.0.8", {"start": v(150.9, 0.85) * mm, "end": v(150.74, -0.13) * mm});
            skArc(sketch, "E11.26.0.0", {"start": v(161.1, 0.85) * mm, "mid": v(160.5, 1.35) * mm, "end": v(159.9, 0.85) * mm});
            skLineSegment(sketch, "E11.26.0.1", {"start": v(161.1, 0.85) * mm, "end": v(161.26, -0.13) * mm});
            skArc(sketch, "E11.26.0.2", {"start": v(155.25, 0) * mm, "mid": v(155.94, -0.75) * mm, "end": v(156.74, -0.13) * mm});
            skArc(sketch, "E11.26.0.3", {"start": v(158.26, -0.13) * mm, "mid": v(159, -0.75) * mm, "end": v(159.74, -0.13) * mm});
            skLineSegment(sketch, "E11.26.0.4", {"start": v(158.1, 0.85) * mm, "end": v(158.26, -0.13) * mm});
            skArc(sketch, "E11.26.0.5", {"start": v(158.1, 0.85) * mm, "mid": v(157.5, 1.35) * mm, "end": v(156.9, 0.85) * mm});
            skLineSegment(sketch, "E11.26.0.6", {"start": v(159.9, 0.85) * mm, "end": v(159.74, -0.13) * mm});
            skArc(sketch, "E11.26.0.7", {"start": v(161.26, -0.13) * mm, "mid": v(162.06, -0.75) * mm, "end": v(162.75, 0) * mm});
            skLineSegment(sketch, "E11.26.0.8", {"start": v(156.9, 0.85) * mm, "end": v(156.74, -0.13) * mm});
            skArc(sketch, "E11.27.0.0", {"start": v(167.1, 0.85) * mm, "mid": v(166.5, 1.35) * mm, "end": v(165.9, 0.85) * mm});
            skLineSegment(sketch, "E11.27.0.1", {"start": v(167.1, 0.85) * mm, "end": v(167.26, -0.13) * mm});
            skArc(sketch, "E11.27.0.2", {"start": v(161.25, 0) * mm, "mid": v(161.94, -0.75) * mm, "end": v(162.74, -0.13) * mm});
            skArc(sketch, "E11.27.0.3", {"start": v(164.26, -0.13) * mm, "mid": v(165, -0.75) * mm, "end": v(165.74, -0.13) * mm});
            skLineSegment(sketch, "E11.27.0.4", {"start": v(164.1, 0.85) * mm, "end": v(164.26, -0.13) * mm});
            skArc(sketch, "E11.27.0.5", {"start": v(164.1, 0.85) * mm, "mid": v(163.5, 1.35) * mm, "end": v(162.9, 0.85) * mm});
            skLineSegment(sketch, "E11.27.0.6", {"start": v(165.9, 0.85) * mm, "end": v(165.74, -0.13) * mm});
            skArc(sketch, "E11.27.0.7", {"start": v(167.26, -0.13) * mm, "mid": v(168.06, -0.75) * mm, "end": v(168.75, 0) * mm});
            skLineSegment(sketch, "E11.27.0.8", {"start": v(162.9, 0.85) * mm, "end": v(162.74, -0.13) * mm});
            skArc(sketch, "E11.28.0.0", {"start": v(173.1, 0.85) * mm, "mid": v(172.5, 1.35) * mm, "end": v(171.9, 0.85) * mm});
            skLineSegment(sketch, "E11.28.0.1", {"start": v(173.1, 0.85) * mm, "end": v(173.26, -0.13) * mm});
            skArc(sketch, "E11.28.0.2", {"start": v(167.25, 0) * mm, "mid": v(167.94, -0.75) * mm, "end": v(168.74, -0.13) * mm});
            skArc(sketch, "E11.28.0.3", {"start": v(170.26, -0.13) * mm, "mid": v(171, -0.75) * mm, "end": v(171.74, -0.13) * mm});
            skLineSegment(sketch, "E11.28.0.4", {"start": v(170.1, 0.85) * mm, "end": v(170.26, -0.13) * mm});
            skArc(sketch, "E11.28.0.5", {"start": v(170.1, 0.85) * mm, "mid": v(169.5, 1.35) * mm, "end": v(168.9, 0.85) * mm});
            skLineSegment(sketch, "E11.28.0.6", {"start": v(171.9, 0.85) * mm, "end": v(171.74, -0.13) * mm});
            skArc(sketch, "E11.28.0.7", {"start": v(173.26, -0.13) * mm, "mid": v(174.06, -0.75) * mm, "end": v(174.75, 0) * mm});
            skLineSegment(sketch, "E11.28.0.8", {"start": v(168.9, 0.85) * mm, "end": v(168.74, -0.13) * mm});
            skArc(sketch, "E11.29.0.0", {"start": v(179.1, 0.85) * mm, "mid": v(178.5, 1.35) * mm, "end": v(177.9, 0.85) * mm});
            skLineSegment(sketch, "E11.29.0.1", {"start": v(179.1, 0.85) * mm, "end": v(179.26, -0.13) * mm});
            skArc(sketch, "E11.29.0.2", {"start": v(173.25, 0) * mm, "mid": v(173.94, -0.75) * mm, "end": v(174.74, -0.13) * mm});
            skArc(sketch, "E11.29.0.3", {"start": v(176.26, -0.13) * mm, "mid": v(177, -0.75) * mm, "end": v(177.74, -0.13) * mm});
            skLineSegment(sketch, "E11.29.0.4", {"start": v(176.1, 0.85) * mm, "end": v(176.26, -0.13) * mm});
            skArc(sketch, "E11.29.0.5", {"start": v(176.1, 0.85) * mm, "mid": v(175.5, 1.35) * mm, "end": v(174.9, 0.85) * mm});
            skLineSegment(sketch, "E11.29.0.6", {"start": v(177.9, 0.85) * mm, "end": v(177.74, -0.13) * mm});
            skArc(sketch, "E11.29.0.7", {"start": v(179.26, -0.13) * mm, "mid": v(180.06, -0.75) * mm, "end": v(180.75, 0) * mm});
            skLineSegment(sketch, "E11.29.0.8", {"start": v(174.9, 0.85) * mm, "end": v(174.74, -0.13) * mm});
            skLineSegment(sketch, "E11.direction1", {"start": v(-0.75, 0) * mm, "end": v(5.25, 0) * mm, "construction": true});
            skLineSegment(sketch, "E12", {"start": v(180.75, 0) * mm, "end": v(180.75, 5) * mm});
            skSolve(sketch);
        }
        {
            var Q0;
            Q0=makeQuery(id+"F0.imprint","IMPRINT",FACE,{"disambiguationData":[TD([[makeQuery(id+"F0.imprint","IMPRINT",EDGE,{"derivedFrom":sQuery(id+"F0.wireOp",EDGE,"hf4xCN9H-XqUV-e8hF-WyFx-ZE3y2IpSfm8S")}),1.0]])]});
            var Q1;
            Q1=makeQuery(id+"F0.imprint","IMPRINT",FACE,{"disambiguationData":[TD([[makeQuery(id+"F0.imprint","IMPRINT",EDGE,{"derivedFrom":sQuery(id+"F0.wireOp",EDGE,"E0")}),1.0]])]});
            extrude(context, id + "F1", {"entities" : qUnion([Q0, Q1]), "endBound" : BoundingType.SYMMETRIC, "depth" : 5 * mm});
        }
        {
            var Q0;
            Q0=makeQuery(id+"F1.opExtrude","CAP_FACE",FACE,{"disambiguationData":[OSD([sQuery(id+"F0.wireOp",EDGE,"E0"),sQuery(id+"F0.wireOp",EDGE,"E1"),sQuery(id+"F0.wireOp",EDGE,"E2"),sQuery(id+"F0.wireOp",EDGE,"E3"),sQuery(id+"F0.wireOp",EDGE,"E4"),sQuery(id+"F0.wireOp",EDGE,"E6"),sQuery(id+"F0.wireOp",EDGE,"E7"),sQuery(id+"F0.wireOp",EDGE,"E8"),sQuery(id+"F0.wireOp",EDGE,"E9"),sQuery(id+"F0.wireOp",EDGE,"E10"),sQuery(id+"F0.wireOp",EDGE,"E11.1.0.0"),sQuery(id+"F0.wireOp",EDGE,"E11.1.0.1"),sQuery(id+"F0.wireOp",EDGE,"E11.1.0.2"),sQuery(id+"F0.wireOp",EDGE,"E11.1.0.3"),sQuery(id+"F0.wireOp",EDGE,"E11.1.0.4"),sQuery(id+"F0.wireOp",EDGE,"E11.1.0.5"),sQuery(id+"F0.wireOp",EDGE,"E11.1.0.6"),sQuery(id+"F0.wireOp",EDGE,"E11.1.0.8"),sQuery(id+"F0.wireOp",EDGE,"E11.2.0.0"),sQuery(id+"F0.wireOp",EDGE,"E11.2.0.1"),sQuery(id+"F0.wireOp",EDGE,"E11.2.0.2"),sQuery(id+"F0.wireOp",EDGE,"E11.2.0.3"),sQuery(id+"F0.wireOp",EDGE,"E11.2.0.4"),sQuery(id+"F0.wireOp",EDGE,"E11.2.0.5"),sQuery(id+"F0.wireOp",EDGE,"E11.2.0.6"),sQuery(id+"F0.wireOp",EDGE,"E11.2.0.8"),sQuery(id+"F0.wireOp",EDGE,"E11.3.0.0"),sQuery(id+"F0.wireOp",EDGE,"E11.3.0.1"),sQuery(id+"F0.wireOp",EDGE,"E11.3.0.2"),sQuery(id+"F0.wireOp",EDGE,"E11.3.0.3"),sQuery(id+"F0.wireOp",EDGE,"E11.3.0.4"),sQuery(id+"F0.wireOp",EDGE,"E11.3.0.5"),sQuery(id+"F0.wireOp",EDGE,"E11.3.0.6"),sQuery(id+"F0.wireOp",EDGE,"E11.3.0.8"),sQuery(id+"F0.wireOp",EDGE,"E11.4.0.0"),sQuery(id+"F0.wireOp",EDGE,"E11.4.0.1"),sQuery(id+"F0.wireOp",EDGE,"E11.4.0.2"),sQuery(id+"F0.wireOp",EDGE,"E11.4.0.3"),sQuery(id+"F0.wireOp",EDGE,"E11.4.0.4"),sQuery(id+"F0.wireOp",EDGE,"E11.4.0.5"),sQuery(id+"F0.wireOp",EDGE,"E11.4.0.6"),sQuery(id+"F0.wireOp",EDGE,"E11.4.0.8"),sQuery(id+"F0.wireOp",EDGE,"E11.5.0.0"),sQuery(id+"F0.wireOp",EDGE,"E11.5.0.1"),sQuery(id+"F0.wireOp",EDGE,"E11.5.0.2"),sQuery(id+"F0.wireOp",EDGE,"E11.5.0.3"),sQuery(id+"F0.wireOp",EDGE,"E11.5.0.4"),sQuery(id+"F0.wireOp",EDGE,"E11.5.0.5"),sQuery(id+"F0.wireOp",EDGE,"E11.5.0.6"),sQuery(id+"F0.wireOp",EDGE,"E11.5.0.8"),sQuery(id+"F0.wireOp",EDGE,"E11.6.0.0"),sQuery(id+"F0.wireOp",EDGE,"E11.6.0.1"),sQuery(id+"F0.wireOp",EDGE,"E11.6.0.2"),sQuery(id+"F0.wireOp",EDGE,"E11.6.0.3"),sQuery(id+"F0.wireOp",EDGE,"E11.6.0.4"),sQuery(id+"F0.wireOp",EDGE,"E11.6.0.5"),sQuery(id+"F0.wireOp",EDGE,"E11.6.0.6"),sQuery(id+"F0.wireOp",EDGE,"E11.6.0.8"),sQuery(id+"F0.wireOp",EDGE,"E11.7.0.0"),sQuery(id+"F0.wireOp",EDGE,"E11.7.0.1"),sQuery(id+"F0.wireOp",EDGE,"E11.7.0.2"),sQuery(id+"F0.wireOp",EDGE,"E11.7.0.3"),sQuery(id+"F0.wireOp",EDGE,"E11.7.0.4"),sQuery(id+"F0.wireOp",EDGE,"E11.7.0.5"),sQuery(id+"F0.wireOp",EDGE,"E11.7.0.6"),sQuery(id+"F0.wireOp",EDGE,"E11.7.0.8"),sQuery(id+"F0.wireOp",EDGE,"E11.8.0.0"),sQuery(id+"F0.wireOp",EDGE,"E11.8.0.1"),sQuery(id+"F0.wireOp",EDGE,"E11.8.0.2"),sQuery(id+"F0.wireOp",EDGE,"E11.8.0.3"),sQuery(id+"F0.wireOp",EDGE,"E11.8.0.4"),sQuery(id+"F0.wireOp",EDGE,"E11.8.0.5"),sQuery(id+"F0.wireOp",EDGE,"E11.8.0.6"),sQuery(id+"F0.wireOp",EDGE,"E11.8.0.8"),sQuery(id+"F0.wireOp",EDGE,"E11.9.0.0"),sQuery(id+"F0.wireOp",EDGE,"E11.9.0.1"),sQuery(id+"F0.wireOp",EDGE,"E11.9.0.2"),sQuery(id+"F0.wireOp",EDGE,"E11.9.0.3"),sQuery(id+"F0.wireOp",EDGE,"E11.9.0.4"),sQuery(id+"F0.wireOp",EDGE,"E11.9.0.5"),sQuery(id+"F0.wireOp",EDGE,"E11.9.0.6"),sQuery(id+"F0.wireOp",EDGE,"E11.9.0.8"),sQuery(id+"F0.wireOp",EDGE,"E11.10.0.0"),sQuery(id+"F0.wireOp",EDGE,"E11.10.0.1"),sQuery(id+"F0.wireOp",EDGE,"E11.10.0.2"),sQuery(id+"F0.wireOp",EDGE,"E11.10.0.3"),sQuery(id+"F0.wireOp",EDGE,"E11.10.0.4"),sQuery(id+"F0.wireOp",EDGE,"E11.10.0.5"),sQuery(id+"F0.wireOp",EDGE,"E11.10.0.6"),sQuery(id+"F0.wireOp",EDGE,"E11.10.0.8"),sQuery(id+"F0.wireOp",EDGE,"E11.11.0.0"),sQuery(id+"F0.wireOp",EDGE,"E11.11.0.1"),sQuery(id+"F0.wireOp",EDGE,"E11.11.0.2"),sQuery(id+"F0.wireOp",EDGE,"E11.11.0.3"),sQuery(id+"F0.wireOp",EDGE,"E11.11.0.4"),sQuery(id+"F0.wireOp",EDGE,"E11.11.0.5"),sQuery(id+"F0.wireOp",EDGE,"E11.11.0.6"),sQuery(id+"F0.wireOp",EDGE,"E11.11.0.8"),sQuery(id+"F0.wireOp",EDGE,"E11.12.0.0"),sQuery(id+"F0.wireOp",EDGE,"E11.12.0.1"),sQuery(id+"F0.wireOp",EDGE,"E11.12.0.2"),sQuery(id+"F0.wireOp",EDGE,"E11.12.0.3"),sQuery(id+"F0.wireOp",EDGE,"E11.12.0.4"),sQuery(id+"F0.wireOp",EDGE,"E11.12.0.5"),sQuery(id+"F0.wireOp",EDGE,"E11.12.0.6"),sQuery(id+"F0.wireOp",EDGE,"E11.12.0.8"),sQuery(id+"F0.wireOp",EDGE,"E11.13.0.0"),sQuery(id+"F0.wireOp",EDGE,"E11.13.0.1"),sQuery(id+"F0.wireOp",EDGE,"E11.13.0.2"),sQuery(id+"F0.wireOp",EDGE,"E11.13.0.3"),sQuery(id+"F0.wireOp",EDGE,"E11.13.0.4"),sQuery(id+"F0.wireOp",EDGE,"E11.13.0.5"),sQuery(id+"F0.wireOp",EDGE,"E11.13.0.6"),sQuery(id+"F0.wireOp",EDGE,"E11.13.0.8"),sQuery(id+"F0.wireOp",EDGE,"E11.14.0.0"),sQuery(id+"F0.wireOp",EDGE,"E11.14.0.1"),sQuery(id+"F0.wireOp",EDGE,"E11.14.0.2"),sQuery(id+"F0.wireOp",EDGE,"E11.14.0.3"),sQuery(id+"F0.wireOp",EDGE,"E11.14.0.4"),sQuery(id+"F0.wireOp",EDGE,"E11.14.0.5"),sQuery(id+"F0.wireOp",EDGE,"E11.14.0.6"),sQuery(id+"F0.wireOp",EDGE,"E11.14.0.8"),sQuery(id+"F0.wireOp",EDGE,"E11.15.0.0"),sQuery(id+"F0.wireOp",EDGE,"E11.15.0.1"),sQuery(id+"F0.wireOp",EDGE,"E11.15.0.2"),sQuery(id+"F0.wireOp",EDGE,"E11.15.0.3"),sQuery(id+"F0.wireOp",EDGE,"E11.15.0.4"),sQuery(id+"F0.wireOp",EDGE,"E11.15.0.5"),sQuery(id+"F0.wireOp",EDGE,"E11.15.0.6"),sQuery(id+"F0.wireOp",EDGE,"E11.15.0.8"),sQuery(id+"F0.wireOp",EDGE,"E11.16.0.0"),sQuery(id+"F0.wireOp",EDGE,"E11.16.0.1"),sQuery(id+"F0.wireOp",EDGE,"E11.16.0.2"),sQuery(id+"F0.wireOp",EDGE,"E11.16.0.3"),sQuery(id+"F0.wireOp",EDGE,"E11.16.0.4"),sQuery(id+"F0.wireOp",EDGE,"E11.16.0.5"),sQuery(id+"F0.wireOp",EDGE,"E11.16.0.6"),sQuery(id+"F0.wireOp",EDGE,"E11.16.0.8"),sQuery(id+"F0.wireOp",EDGE,"E11.17.0.0"),sQuery(id+"F0.wireOp",EDGE,"E11.17.0.1"),sQuery(id+"F0.wireOp",EDGE,"E11.17.0.2"),sQuery(id+"F0.wireOp",EDGE,"E11.17.0.3"),sQuery(id+"F0.wireOp",EDGE,"E11.17.0.4"),sQuery(id+"F0.wireOp",EDGE,"E11.17.0.5"),sQuery(id+"F0.wireOp",EDGE,"E11.17.0.6"),sQuery(id+"F0.wireOp",EDGE,"E11.17.0.8"),sQuery(id+"F0.wireOp",EDGE,"E11.18.0.0"),sQuery(id+"F0.wireOp",EDGE,"E11.18.0.1"),sQuery(id+"F0.wireOp",EDGE,"E11.18.0.2"),sQuery(id+"F0.wireOp",EDGE,"E11.18.0.3"),sQuery(id+"F0.wireOp",EDGE,"E11.18.0.4"),sQuery(id+"F0.wireOp",EDGE,"E11.18.0.5"),sQuery(id+"F0.wireOp",EDGE,"E11.18.0.6"),sQuery(id+"F0.wireOp",EDGE,"E11.18.0.8"),sQuery(id+"F0.wireOp",EDGE,"E11.19.0.0"),sQuery(id+"F0.wireOp",EDGE,"E11.19.0.1"),sQuery(id+"F0.wireOp",EDGE,"E11.19.0.2"),sQuery(id+"F0.wireOp",EDGE,"E11.19.0.3"),sQuery(id+"F0.wireOp",EDGE,"E11.19.0.4"),sQuery(id+"F0.wireOp",EDGE,"E11.19.0.5"),sQuery(id+"F0.wireOp",EDGE,"E11.19.0.6"),sQuery(id+"F0.wireOp",EDGE,"E11.19.0.8"),sQuery(id+"F0.wireOp",EDGE,"E11.20.0.0"),sQuery(id+"F0.wireOp",EDGE,"E11.20.0.1"),sQuery(id+"F0.wireOp",EDGE,"E11.20.0.2"),sQuery(id+"F0.wireOp",EDGE,"E11.20.0.3"),sQuery(id+"F0.wireOp",EDGE,"E11.20.0.4"),sQuery(id+"F0.wireOp",EDGE,"E11.20.0.5"),sQuery(id+"F0.wireOp",EDGE,"E11.20.0.6"),sQuery(id+"F0.wireOp",EDGE,"E11.20.0.8"),sQuery(id+"F0.wireOp",EDGE,"E11.21.0.0"),sQuery(id+"F0.wireOp",EDGE,"E11.21.0.1"),sQuery(id+"F0.wireOp",EDGE,"E11.21.0.2"),sQuery(id+"F0.wireOp",EDGE,"E11.21.0.3"),sQuery(id+"F0.wireOp",EDGE,"E11.21.0.4"),sQuery(id+"F0.wireOp",EDGE,"E11.21.0.5"),sQuery(id+"F0.wireOp",EDGE,"E11.21.0.6"),sQuery(id+"F0.wireOp",EDGE,"E11.21.0.8"),sQuery(id+"F0.wireOp",EDGE,"E11.22.0.0"),sQuery(id+"F0.wireOp",EDGE,"E11.22.0.1"),sQuery(id+"F0.wireOp",EDGE,"E11.22.0.2"),sQuery(id+"F0.wireOp",EDGE,"E11.22.0.3"),sQuery(id+"F0.wireOp",EDGE,"E11.22.0.4"),sQuery(id+"F0.wireOp",EDGE,"E11.22.0.5"),sQuery(id+"F0.wireOp",EDGE,"E11.22.0.6"),sQuery(id+"F0.wireOp",EDGE,"E11.22.0.8"),sQuery(id+"F0.wireOp",EDGE,"E11.23.0.0"),sQuery(id+"F0.wireOp",EDGE,"E11.23.0.1"),sQuery(id+"F0.wireOp",EDGE,"E11.23.0.2"),sQuery(id+"F0.wireOp",EDGE,"E11.23.0.3"),sQuery(id+"F0.wireOp",EDGE,"E11.23.0.4"),sQuery(id+"F0.wireOp",EDGE,"E11.23.0.5"),sQuery(id+"F0.wireOp",EDGE,"E11.23.0.6"),sQuery(id+"F0.wireOp",EDGE,"E11.23.0.8"),sQuery(id+"F0.wireOp",EDGE,"E11.24.0.0"),sQuery(id+"F0.wireOp",EDGE,"E11.24.0.1"),sQuery(id+"F0.wireOp",EDGE,"E11.24.0.2"),sQuery(id+"F0.wireOp",EDGE,"E11.24.0.3"),sQuery(id+"F0.wireOp",EDGE,"E11.24.0.4"),sQuery(id+"F0.wireOp",EDGE,"E11.24.0.5"),sQuery(id+"F0.wireOp",EDGE,"E11.24.0.6"),sQuery(id+"F0.wireOp",EDGE,"E11.24.0.8"),sQuery(id+"F0.wireOp",EDGE,"E11.25.0.0"),sQuery(id+"F0.wireOp",EDGE,"E11.25.0.1"),sQuery(id+"F0.wireOp",EDGE,"E11.25.0.2"),sQuery(id+"F0.wireOp",EDGE,"E11.25.0.3"),sQuery(id+"F0.wireOp",EDGE,"E11.25.0.4"),sQuery(id+"F0.wireOp",EDGE,"E11.25.0.5"),sQuery(id+"F0.wireOp",EDGE,"E11.25.0.6"),sQuery(id+"F0.wireOp",EDGE,"E11.25.0.8"),sQuery(id+"F0.wireOp",EDGE,"E11.26.0.0"),sQuery(id+"F0.wireOp",EDGE,"E11.26.0.1"),sQuery(id+"F0.wireOp",EDGE,"E11.26.0.2"),sQuery(id+"F0.wireOp",EDGE,"E11.26.0.3"),sQuery(id+"F0.wireOp",EDGE,"E11.26.0.4"),sQuery(id+"F0.wireOp",EDGE,"E11.26.0.5"),sQuery(id+"F0.wireOp",EDGE,"E11.26.0.6"),sQuery(id+"F0.wireOp",EDGE,"E11.26.0.8"),sQuery(id+"F0.wireOp",EDGE,"E11.27.0.0"),sQuery(id+"F0.wireOp",EDGE,"E11.27.0.1"),sQuery(id+"F0.wireOp",EDGE,"E11.27.0.2"),sQuery(id+"F0.wireOp",EDGE,"E11.27.0.3"),sQuery(id+"F0.wireOp",EDGE,"E11.27.0.4"),sQuery(id+"F0.wireOp",EDGE,"E11.27.0.5"),sQuery(id+"F0.wireOp",EDGE,"E11.27.0.6"),sQuery(id+"F0.wireOp",EDGE,"E11.27.0.8"),sQuery(id+"F0.wireOp",EDGE,"E11.28.0.0"),sQuery(id+"F0.wireOp",EDGE,"E11.28.0.1"),sQuery(id+"F0.wireOp",EDGE,"E11.28.0.2"),sQuery(id+"F0.wireOp",EDGE,"E11.28.0.3"),sQuery(id+"F0.wireOp",EDGE,"E11.28.0.4"),sQuery(id+"F0.wireOp",EDGE,"E11.28.0.5"),sQuery(id+"F0.wireOp",EDGE,"E11.28.0.6"),sQuery(id+"F0.wireOp",EDGE,"E11.28.0.8"),sQuery(id+"F0.wireOp",EDGE,"E11.29.0.0"),sQuery(id+"F0.wireOp",EDGE,"E11.29.0.1"),sQuery(id+"F0.wireOp",EDGE,"E11.29.0.2"),sQuery(id+"F0.wireOp",EDGE,"E11.29.0.3"),sQuery(id+"F0.wireOp",EDGE,"E11.29.0.4"),sQuery(id+"F0.wireOp",EDGE,"E11.29.0.5"),sQuery(id+"F0.wireOp",EDGE,"E11.29.0.6"),sQuery(id+"F0.wireOp",EDGE,"E11.29.0.7"),sQuery(id+"F0.wireOp",EDGE,"E11.29.0.8"),sQuery(id+"F0.wireOp",EDGE,"E12")])],"isStart":false});
            var Q1;
            Q1=makeQuery(id+"F1.opExtrude","CAP_FACE",FACE,{"disambiguationData":[OSD([sQuery(id+"F0.wireOp",EDGE,"E0"),sQuery(id+"F0.wireOp",EDGE,"E1"),sQuery(id+"F0.wireOp",EDGE,"E2"),sQuery(id+"F0.wireOp",EDGE,"E3"),sQuery(id+"F0.wireOp",EDGE,"E4"),sQuery(id+"F0.wireOp",EDGE,"E6"),sQuery(id+"F0.wireOp",EDGE,"E7"),sQuery(id+"F0.wireOp",EDGE,"E8"),sQuery(id+"F0.wireOp",EDGE,"E9"),sQuery(id+"F0.wireOp",EDGE,"E10"),sQuery(id+"F0.wireOp",EDGE,"E11.1.0.0"),sQuery(id+"F0.wireOp",EDGE,"E11.1.0.1"),sQuery(id+"F0.wireOp",EDGE,"E11.1.0.2"),sQuery(id+"F0.wireOp",EDGE,"E11.1.0.3"),sQuery(id+"F0.wireOp",EDGE,"E11.1.0.4"),sQuery(id+"F0.wireOp",EDGE,"E11.1.0.5"),sQuery(id+"F0.wireOp",EDGE,"E11.1.0.6"),sQuery(id+"F0.wireOp",EDGE,"E11.1.0.8"),sQuery(id+"F0.wireOp",EDGE,"E11.2.0.0"),sQuery(id+"F0.wireOp",EDGE,"E11.2.0.1"),sQuery(id+"F0.wireOp",EDGE,"E11.2.0.2"),sQuery(id+"F0.wireOp",EDGE,"E11.2.0.3"),sQuery(id+"F0.wireOp",EDGE,"E11.2.0.4"),sQuery(id+"F0.wireOp",EDGE,"E11.2.0.5"),sQuery(id+"F0.wireOp",EDGE,"E11.2.0.6"),sQuery(id+"F0.wireOp",EDGE,"E11.2.0.8"),sQuery(id+"F0.wireOp",EDGE,"E11.3.0.0"),sQuery(id+"F0.wireOp",EDGE,"E11.3.0.1"),sQuery(id+"F0.wireOp",EDGE,"E11.3.0.2"),sQuery(id+"F0.wireOp",EDGE,"E11.3.0.3"),sQuery(id+"F0.wireOp",EDGE,"E11.3.0.4"),sQuery(id+"F0.wireOp",EDGE,"E11.3.0.5"),sQuery(id+"F0.wireOp",EDGE,"E11.3.0.6"),sQuery(id+"F0.wireOp",EDGE,"E11.3.0.8"),sQuery(id+"F0.wireOp",EDGE,"E11.4.0.0"),sQuery(id+"F0.wireOp",EDGE,"E11.4.0.1"),sQuery(id+"F0.wireOp",EDGE,"E11.4.0.2"),sQuery(id+"F0.wireOp",EDGE,"E11.4.0.3"),sQuery(id+"F0.wireOp",EDGE,"E11.4.0.4"),sQuery(id+"F0.wireOp",EDGE,"E11.4.0.5"),sQuery(id+"F0.wireOp",EDGE,"E11.4.0.6"),sQuery(id+"F0.wireOp",EDGE,"E11.4.0.8"),sQuery(id+"F0.wireOp",EDGE,"E11.5.0.0"),sQuery(id+"F0.wireOp",EDGE,"E11.5.0.1"),sQuery(id+"F0.wireOp",EDGE,"E11.5.0.2"),sQuery(id+"F0.wireOp",EDGE,"E11.5.0.3"),sQuery(id+"F0.wireOp",EDGE,"E11.5.0.4"),sQuery(id+"F0.wireOp",EDGE,"E11.5.0.5"),sQuery(id+"F0.wireOp",EDGE,"E11.5.0.6"),sQuery(id+"F0.wireOp",EDGE,"E11.5.0.8"),sQuery(id+"F0.wireOp",EDGE,"E11.6.0.0"),sQuery(id+"F0.wireOp",EDGE,"E11.6.0.1"),sQuery(id+"F0.wireOp",EDGE,"E11.6.0.2"),sQuery(id+"F0.wireOp",EDGE,"E11.6.0.3"),sQuery(id+"F0.wireOp",EDGE,"E11.6.0.4"),sQuery(id+"F0.wireOp",EDGE,"E11.6.0.5"),sQuery(id+"F0.wireOp",EDGE,"E11.6.0.6"),sQuery(id+"F0.wireOp",EDGE,"E11.6.0.8"),sQuery(id+"F0.wireOp",EDGE,"E11.7.0.0"),sQuery(id+"F0.wireOp",EDGE,"E11.7.0.1"),sQuery(id+"F0.wireOp",EDGE,"E11.7.0.2"),sQuery(id+"F0.wireOp",EDGE,"E11.7.0.3"),sQuery(id+"F0.wireOp",EDGE,"E11.7.0.4"),sQuery(id+"F0.wireOp",EDGE,"E11.7.0.5"),sQuery(id+"F0.wireOp",EDGE,"E11.7.0.6"),sQuery(id+"F0.wireOp",EDGE,"E11.7.0.8"),sQuery(id+"F0.wireOp",EDGE,"E11.8.0.0"),sQuery(id+"F0.wireOp",EDGE,"E11.8.0.1"),sQuery(id+"F0.wireOp",EDGE,"E11.8.0.2"),sQuery(id+"F0.wireOp",EDGE,"E11.8.0.3"),sQuery(id+"F0.wireOp",EDGE,"E11.8.0.4"),sQuery(id+"F0.wireOp",EDGE,"E11.8.0.5"),sQuery(id+"F0.wireOp",EDGE,"E11.8.0.6"),sQuery(id+"F0.wireOp",EDGE,"E11.8.0.8"),sQuery(id+"F0.wireOp",EDGE,"E11.9.0.0"),sQuery(id+"F0.wireOp",EDGE,"E11.9.0.1"),sQuery(id+"F0.wireOp",EDGE,"E11.9.0.2"),sQuery(id+"F0.wireOp",EDGE,"E11.9.0.3"),sQuery(id+"F0.wireOp",EDGE,"E11.9.0.4"),sQuery(id+"F0.wireOp",EDGE,"E11.9.0.5"),sQuery(id+"F0.wireOp",EDGE,"E11.9.0.6"),sQuery(id+"F0.wireOp",EDGE,"E11.9.0.8"),sQuery(id+"F0.wireOp",EDGE,"E11.10.0.0"),sQuery(id+"F0.wireOp",EDGE,"E11.10.0.1"),sQuery(id+"F0.wireOp",EDGE,"E11.10.0.2"),sQuery(id+"F0.wireOp",EDGE,"E11.10.0.3"),sQuery(id+"F0.wireOp",EDGE,"E11.10.0.4"),sQuery(id+"F0.wireOp",EDGE,"E11.10.0.5"),sQuery(id+"F0.wireOp",EDGE,"E11.10.0.6"),sQuery(id+"F0.wireOp",EDGE,"E11.10.0.8"),sQuery(id+"F0.wireOp",EDGE,"E11.11.0.0"),sQuery(id+"F0.wireOp",EDGE,"E11.11.0.1"),sQuery(id+"F0.wireOp",EDGE,"E11.11.0.2"),sQuery(id+"F0.wireOp",EDGE,"E11.11.0.3"),sQuery(id+"F0.wireOp",EDGE,"E11.11.0.4"),sQuery(id+"F0.wireOp",EDGE,"E11.11.0.5"),sQuery(id+"F0.wireOp",EDGE,"E11.11.0.6"),sQuery(id+"F0.wireOp",EDGE,"E11.11.0.8"),sQuery(id+"F0.wireOp",EDGE,"E11.12.0.0"),sQuery(id+"F0.wireOp",EDGE,"E11.12.0.1"),sQuery(id+"F0.wireOp",EDGE,"E11.12.0.2"),sQuery(id+"F0.wireOp",EDGE,"E11.12.0.3"),sQuery(id+"F0.wireOp",EDGE,"E11.12.0.4"),sQuery(id+"F0.wireOp",EDGE,"E11.12.0.5"),sQuery(id+"F0.wireOp",EDGE,"E11.12.0.6"),sQuery(id+"F0.wireOp",EDGE,"E11.12.0.8"),sQuery(id+"F0.wireOp",EDGE,"E11.13.0.0"),sQuery(id+"F0.wireOp",EDGE,"E11.13.0.1"),sQuery(id+"F0.wireOp",EDGE,"E11.13.0.2"),sQuery(id+"F0.wireOp",EDGE,"E11.13.0.3"),sQuery(id+"F0.wireOp",EDGE,"E11.13.0.4"),sQuery(id+"F0.wireOp",EDGE,"E11.13.0.5"),sQuery(id+"F0.wireOp",EDGE,"E11.13.0.6"),sQuery(id+"F0.wireOp",EDGE,"E11.13.0.8"),sQuery(id+"F0.wireOp",EDGE,"E11.14.0.0"),sQuery(id+"F0.wireOp",EDGE,"E11.14.0.1"),sQuery(id+"F0.wireOp",EDGE,"E11.14.0.2"),sQuery(id+"F0.wireOp",EDGE,"E11.14.0.3"),sQuery(id+"F0.wireOp",EDGE,"E11.14.0.4"),sQuery(id+"F0.wireOp",EDGE,"E11.14.0.5"),sQuery(id+"F0.wireOp",EDGE,"E11.14.0.6"),sQuery(id+"F0.wireOp",EDGE,"E11.14.0.8"),sQuery(id+"F0.wireOp",EDGE,"E11.15.0.0"),sQuery(id+"F0.wireOp",EDGE,"E11.15.0.1"),sQuery(id+"F0.wireOp",EDGE,"E11.15.0.2"),sQuery(id+"F0.wireOp",EDGE,"E11.15.0.3"),sQuery(id+"F0.wireOp",EDGE,"E11.15.0.4"),sQuery(id+"F0.wireOp",EDGE,"E11.15.0.5"),sQuery(id+"F0.wireOp",EDGE,"E11.15.0.6"),sQuery(id+"F0.wireOp",EDGE,"E11.15.0.8"),sQuery(id+"F0.wireOp",EDGE,"E11.16.0.0"),sQuery(id+"F0.wireOp",EDGE,"E11.16.0.1"),sQuery(id+"F0.wireOp",EDGE,"E11.16.0.2"),sQuery(id+"F0.wireOp",EDGE,"E11.16.0.3"),sQuery(id+"F0.wireOp",EDGE,"E11.16.0.4"),sQuery(id+"F0.wireOp",EDGE,"E11.16.0.5"),sQuery(id+"F0.wireOp",EDGE,"E11.16.0.6"),sQuery(id+"F0.wireOp",EDGE,"E11.16.0.8"),sQuery(id+"F0.wireOp",EDGE,"E11.17.0.0"),sQuery(id+"F0.wireOp",EDGE,"E11.17.0.1"),sQuery(id+"F0.wireOp",EDGE,"E11.17.0.2"),sQuery(id+"F0.wireOp",EDGE,"E11.17.0.3"),sQuery(id+"F0.wireOp",EDGE,"E11.17.0.4"),sQuery(id+"F0.wireOp",EDGE,"E11.17.0.5"),sQuery(id+"F0.wireOp",EDGE,"E11.17.0.6"),sQuery(id+"F0.wireOp",EDGE,"E11.17.0.8"),sQuery(id+"F0.wireOp",EDGE,"E11.18.0.0"),sQuery(id+"F0.wireOp",EDGE,"E11.18.0.1"),sQuery(id+"F0.wireOp",EDGE,"E11.18.0.2"),sQuery(id+"F0.wireOp",EDGE,"E11.18.0.3"),sQuery(id+"F0.wireOp",EDGE,"E11.18.0.4"),sQuery(id+"F0.wireOp",EDGE,"E11.18.0.5"),sQuery(id+"F0.wireOp",EDGE,"E11.18.0.6"),sQuery(id+"F0.wireOp",EDGE,"E11.18.0.8"),sQuery(id+"F0.wireOp",EDGE,"E11.19.0.0"),sQuery(id+"F0.wireOp",EDGE,"E11.19.0.1"),sQuery(id+"F0.wireOp",EDGE,"E11.19.0.2"),sQuery(id+"F0.wireOp",EDGE,"E11.19.0.3"),sQuery(id+"F0.wireOp",EDGE,"E11.19.0.4"),sQuery(id+"F0.wireOp",EDGE,"E11.19.0.5"),sQuery(id+"F0.wireOp",EDGE,"E11.19.0.6"),sQuery(id+"F0.wireOp",EDGE,"E11.19.0.8"),sQuery(id+"F0.wireOp",EDGE,"E11.20.0.0"),sQuery(id+"F0.wireOp",EDGE,"E11.20.0.1"),sQuery(id+"F0.wireOp",EDGE,"E11.20.0.2"),sQuery(id+"F0.wireOp",EDGE,"E11.20.0.3"),sQuery(id+"F0.wireOp",EDGE,"E11.20.0.4"),sQuery(id+"F0.wireOp",EDGE,"E11.20.0.5"),sQuery(id+"F0.wireOp",EDGE,"E11.20.0.6"),sQuery(id+"F0.wireOp",EDGE,"E11.20.0.8"),sQuery(id+"F0.wireOp",EDGE,"E11.21.0.0"),sQuery(id+"F0.wireOp",EDGE,"E11.21.0.1"),sQuery(id+"F0.wireOp",EDGE,"E11.21.0.2"),sQuery(id+"F0.wireOp",EDGE,"E11.21.0.3"),sQuery(id+"F0.wireOp",EDGE,"E11.21.0.4"),sQuery(id+"F0.wireOp",EDGE,"E11.21.0.5"),sQuery(id+"F0.wireOp",EDGE,"E11.21.0.6"),sQuery(id+"F0.wireOp",EDGE,"E11.21.0.8"),sQuery(id+"F0.wireOp",EDGE,"E11.22.0.0"),sQuery(id+"F0.wireOp",EDGE,"E11.22.0.1"),sQuery(id+"F0.wireOp",EDGE,"E11.22.0.2"),sQuery(id+"F0.wireOp",EDGE,"E11.22.0.3"),sQuery(id+"F0.wireOp",EDGE,"E11.22.0.4"),sQuery(id+"F0.wireOp",EDGE,"E11.22.0.5"),sQuery(id+"F0.wireOp",EDGE,"E11.22.0.6"),sQuery(id+"F0.wireOp",EDGE,"E11.22.0.8"),sQuery(id+"F0.wireOp",EDGE,"E11.23.0.0"),sQuery(id+"F0.wireOp",EDGE,"E11.23.0.1"),sQuery(id+"F0.wireOp",EDGE,"E11.23.0.2"),sQuery(id+"F0.wireOp",EDGE,"E11.23.0.3"),sQuery(id+"F0.wireOp",EDGE,"E11.23.0.4"),sQuery(id+"F0.wireOp",EDGE,"E11.23.0.5"),sQuery(id+"F0.wireOp",EDGE,"E11.23.0.6"),sQuery(id+"F0.wireOp",EDGE,"E11.23.0.8"),sQuery(id+"F0.wireOp",EDGE,"E11.24.0.0"),sQuery(id+"F0.wireOp",EDGE,"E11.24.0.1"),sQuery(id+"F0.wireOp",EDGE,"E11.24.0.2"),sQuery(id+"F0.wireOp",EDGE,"E11.24.0.3"),sQuery(id+"F0.wireOp",EDGE,"E11.24.0.4"),sQuery(id+"F0.wireOp",EDGE,"E11.24.0.5"),sQuery(id+"F0.wireOp",EDGE,"E11.24.0.6"),sQuery(id+"F0.wireOp",EDGE,"E11.24.0.8"),sQuery(id+"F0.wireOp",EDGE,"E11.25.0.0"),sQuery(id+"F0.wireOp",EDGE,"E11.25.0.1"),sQuery(id+"F0.wireOp",EDGE,"E11.25.0.2"),sQuery(id+"F0.wireOp",EDGE,"E11.25.0.3"),sQuery(id+"F0.wireOp",EDGE,"E11.25.0.4"),sQuery(id+"F0.wireOp",EDGE,"E11.25.0.5"),sQuery(id+"F0.wireOp",EDGE,"E11.25.0.6"),sQuery(id+"F0.wireOp",EDGE,"E11.25.0.8"),sQuery(id+"F0.wireOp",EDGE,"E11.26.0.0"),sQuery(id+"F0.wireOp",EDGE,"E11.26.0.1"),sQuery(id+"F0.wireOp",EDGE,"E11.26.0.2"),sQuery(id+"F0.wireOp",EDGE,"E11.26.0.3"),sQuery(id+"F0.wireOp",EDGE,"E11.26.0.4"),sQuery(id+"F0.wireOp",EDGE,"E11.26.0.5"),sQuery(id+"F0.wireOp",EDGE,"E11.26.0.6"),sQuery(id+"F0.wireOp",EDGE,"E11.26.0.8"),sQuery(id+"F0.wireOp",EDGE,"E11.27.0.0"),sQuery(id+"F0.wireOp",EDGE,"E11.27.0.1"),sQuery(id+"F0.wireOp",EDGE,"E11.27.0.2"),sQuery(id+"F0.wireOp",EDGE,"E11.27.0.3"),sQuery(id+"F0.wireOp",EDGE,"E11.27.0.4"),sQuery(id+"F0.wireOp",EDGE,"E11.27.0.5"),sQuery(id+"F0.wireOp",EDGE,"E11.27.0.6"),sQuery(id+"F0.wireOp",EDGE,"E11.27.0.8"),sQuery(id+"F0.wireOp",EDGE,"E11.28.0.0"),sQuery(id+"F0.wireOp",EDGE,"E11.28.0.1"),sQuery(id+"F0.wireOp",EDGE,"E11.28.0.2"),sQuery(id+"F0.wireOp",EDGE,"E11.28.0.3"),sQuery(id+"F0.wireOp",EDGE,"E11.28.0.4"),sQuery(id+"F0.wireOp",EDGE,"E11.28.0.5"),sQuery(id+"F0.wireOp",EDGE,"E11.28.0.6"),sQuery(id+"F0.wireOp",EDGE,"E11.28.0.8"),sQuery(id+"F0.wireOp",EDGE,"E11.29.0.0"),sQuery(id+"F0.wireOp",EDGE,"E11.29.0.1"),sQuery(id+"F0.wireOp",EDGE,"E11.29.0.2"),sQuery(id+"F0.wireOp",EDGE,"E11.29.0.3"),sQuery(id+"F0.wireOp",EDGE,"E11.29.0.4"),sQuery(id+"F0.wireOp",EDGE,"E11.29.0.5"),sQuery(id+"F0.wireOp",EDGE,"E11.29.0.6"),sQuery(id+"F0.wireOp",EDGE,"E11.29.0.7"),sQuery(id+"F0.wireOp",EDGE,"E11.29.0.8"),sQuery(id+"F0.wireOp",EDGE,"E12")])],"isStart":true});
            fillet(context, id + "F2", {"entities" : qUnion([Q0, Q1]), "radius" : 0.5 * mm, "tangentPropagation" : true, "rho" : 0.5, "crossSection" : FilletCrossSection.CONIC, "allowEdgeOverflow" : false});
        }
    });
